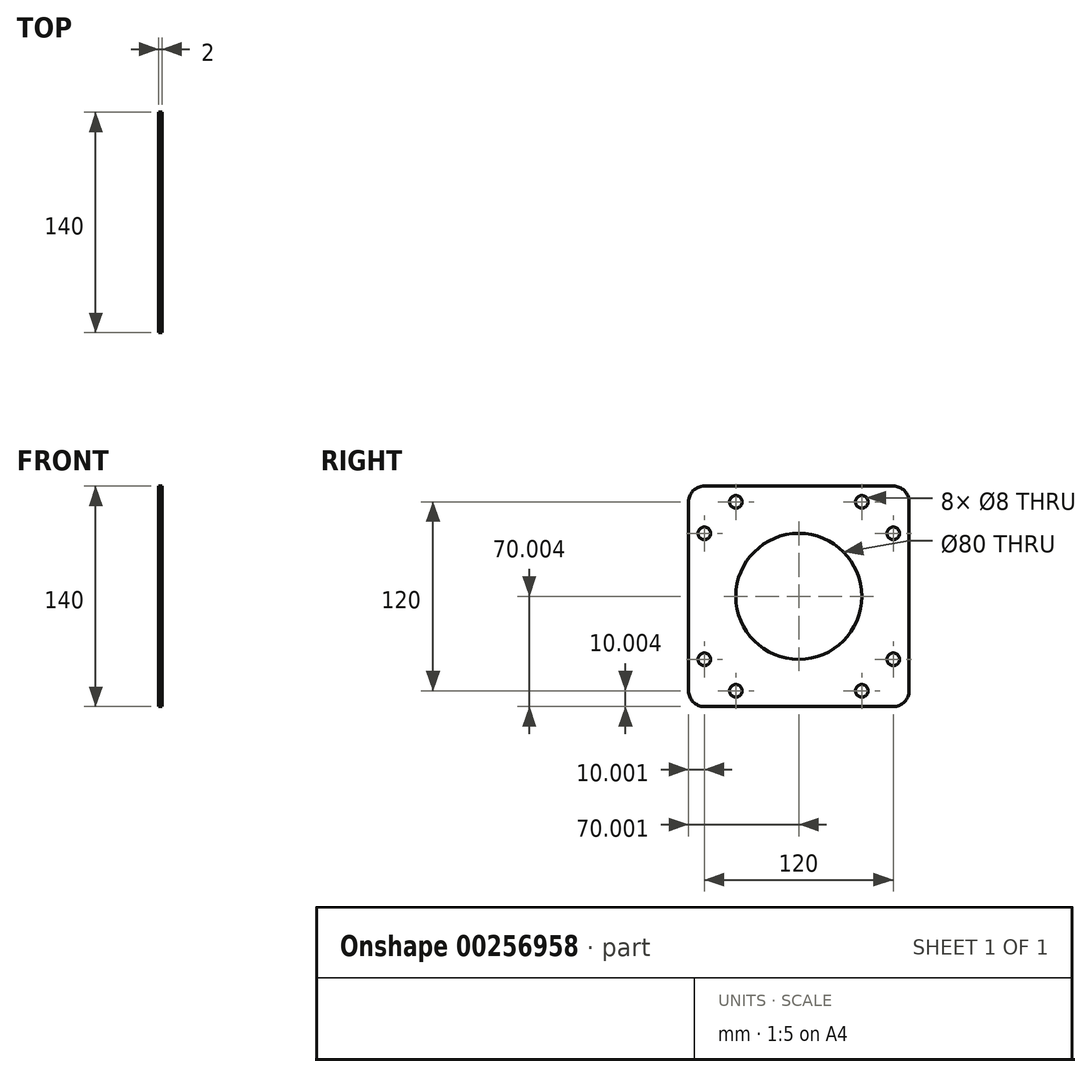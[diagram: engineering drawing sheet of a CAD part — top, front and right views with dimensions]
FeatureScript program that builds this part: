
annotation { "Feature Type Name" : "Feature", "Feature Type Description" : "" }
export const myFeature = defineFeature(function(context is Context, id is Id, definition is map)
    precondition{}
    {
        {
            var Q0;
            Q0=qCreatedBy(makeId("Right.planeOp"),FACE);
            var sketch = newSketch(context, id + "F0", { "sketchPlane" : qUnion([Q0])});
            skArc(sketch, "E0", {"start": v(-63.53, 73.82) * mm, "mid": v(-70.6, 70.9) * mm, "end": v(-73.53, 63.82) * mm});
            skLineSegment(sketch, "E1", {"start": v(-63.53, 73.82) * mm, "end": v(56.47, 73.82) * mm});
            skArc(sketch, "E2", {"start": v(66.47, 63.82) * mm, "mid": v(63.54, 70.9) * mm, "end": v(56.47, 73.82) * mm});
            skLineSegment(sketch, "E3", {"start": v(56.47, 63.82) * mm, "end": v(56.47, 73.82) * mm, "construction": true});
            skLineSegment(sketch, "E4", {"start": v(-63.53, 73.82) * mm, "end": v(-63.53, 63.82) * mm, "construction": true});
            skLineSegment(sketch, "E5", {"start": v(-73.53, 63.82) * mm, "end": v(-73.53, -56.18) * mm});
            skArc(sketch, "E6", {"start": v(-73.53, -56.18) * mm, "mid": v(-70.6, -63.25) * mm, "end": v(-63.53, -66.18) * mm});
            skArc(sketch, "E7", {"start": v(56.47, -66.18) * mm, "mid": v(63.54, -63.25) * mm, "end": v(66.47, -56.18) * mm});
            skLineSegment(sketch, "E8", {"start": v(-63.53, -66.18) * mm, "end": v(56.47, -66.18) * mm});
            skLineSegment(sketch, "E9", {"start": v(66.47, 63.82) * mm, "end": v(66.47, -56.18) * mm});
            skLineSegment(sketch, "E10", {"start": v(-63.53, -56.18) * mm, "end": v(-73.53, -56.18) * mm, "construction": true});
            skLineSegment(sketch, "E11", {"start": v(-63.53, -56.18) * mm, "end": v(-63.53, -66.18) * mm, "construction": true});
            skLineSegment(sketch, "E12", {"start": v(56.47, -56.18) * mm, "end": v(56.47, -66.18) * mm, "construction": true});
            skLineSegment(sketch, "E13", {"start": v(56.47, -66.18) * mm, "end": v(56.47, -56.18) * mm, "construction": true});
            skLineSegment(sketch, "E14", {"start": v(56.47, -56.18) * mm, "end": v(66.47, -56.18) * mm, "construction": true});
            skLineSegment(sketch, "E15", {"start": v(56.47, 63.82) * mm, "end": v(66.47, 63.82) * mm, "construction": true});
            skLineSegment(sketch, "E16", {"start": v(-73.53, 63.82) * mm, "end": v(-63.53, 63.82) * mm, "construction": true});
            skSolve(sketch);
        }
        {
            var Q0;
            Q0=makeQuery(id+"F0.imprint","IMPRINT",FACE,{"disambiguationData":[TD([[makeQuery(id+"F0.imprint","IMPRINT",EDGE,{"derivedFrom":sQuery(id+"F0.wireOp",EDGE,"E0")}),1.0]])]});
            extrude(context, id + "F1", {"entities" : qUnion([Q0]), "depth" : 2 * mm});
        }
        {
            var Q0;
            Q0=makeQuery(id+"F1.opExtrude","CAP_FACE",FACE,{"disambiguationData":[OSD([sQuery(id+"F0.wireOp",EDGE,"E0"),sQuery(id+"F0.wireOp",EDGE,"E1"),sQuery(id+"F0.wireOp",EDGE,"E2"),sQuery(id+"F0.wireOp",EDGE,"E5"),sQuery(id+"F0.wireOp",EDGE,"E6"),sQuery(id+"F0.wireOp",EDGE,"E7"),sQuery(id+"F0.wireOp",EDGE,"E8"),sQuery(id+"F0.wireOp",EDGE,"E9")])],"isStart":false});
            var sketch = newSketch(context, id + "F2", { "sketchPlane" : qUnion([Q0])});
            skCircle(sketch, "E17", {"center": v(-63.53, 43.82) * mm, "radius": 4 * mm});
            skLineSegment(sketch, "E18", {"start": v(-3.53, 73.82) * mm, "end": v(-3.53, -66.18) * mm, "construction": true});
            skLineSegment(sketch, "E19", {"start": v(66.47, 3.82) * mm, "end": v(-73.53, 3.82) * mm, "construction": true});
            skCircle(sketch, "E20", {"center": v(-43.53, 63.82) * mm, "radius": 4 * mm});
            skCircle(sketch, "E21.1.0", {"center": v(-63.53, -36.18) * mm, "radius": 4 * mm});
            skCircle(sketch, "E21.1.1", {"center": v(-43.53, -56.18) * mm, "radius": 4 * mm});
            skCircle(sketch, "E21.2.0", {"center": v(36.47, -56.18) * mm, "radius": 4 * mm});
            skCircle(sketch, "E21.2.1", {"center": v(56.47, -36.18) * mm, "radius": 4 * mm});
            skCircle(sketch, "E21.3.0", {"center": v(56.47, 43.82) * mm, "radius": 4 * mm});
            skCircle(sketch, "E21.3.1", {"center": v(36.47, 63.82) * mm, "radius": 4 * mm});
            skPoint(sketch, "E21.center", {"position": v(-3.53, 3.82) * mm});
            skCircle(sketch, "E22", {"center": v(-3.53, 3.82) * mm, "radius": 40 * mm});
            skSolve(sketch);
        }
        {
            var Q0;
            Q0 = qSketchRegion(id + "F2", true);
            extrude(context, id + "F3", {"entities" : qUnion([Q0]), "operationType" : NewBodyOperationType.REMOVE, "endBound" : BoundingType.UP_TO_NEXT, "oppositeDirection" : true, "depth" : 25 * mm});
        }
    });
